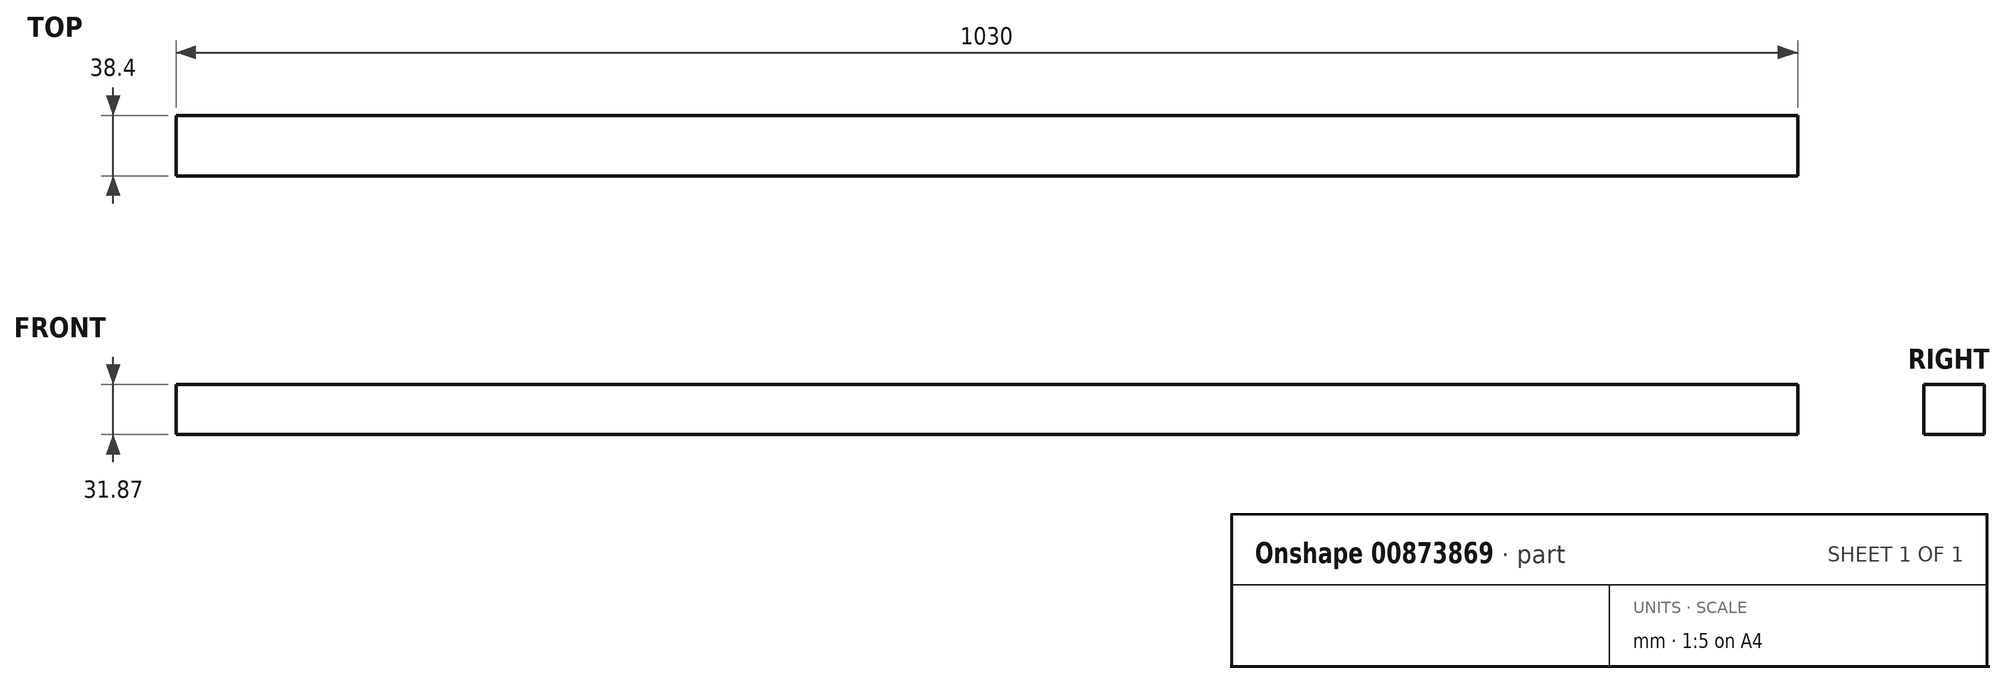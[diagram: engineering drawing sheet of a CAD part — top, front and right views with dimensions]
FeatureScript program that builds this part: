
annotation { "Feature Type Name" : "Feature", "Feature Type Description" : "" }
export const myFeature = defineFeature(function(context is Context, id is Id, definition is map)
    precondition{}
    {
        {
            var Q0;
            Q0=qCreatedBy(makeId("Right.planeOp"),FACE);
            var sketch = newSketch(context, id + "F0", { "sketchPlane" : qUnion([Q0])});
            skLineSegment(sketch, "E0.bottom", {"start": v(0, 0) * mm, "end": v(38.4, 0) * mm});
            skLineSegment(sketch, "E0.top", {"start": v(0, 31.87) * mm, "end": v(38.4, 31.87) * mm});
            skLineSegment(sketch, "E0.left", {"start": v(0, 0) * mm, "end": v(0, 31.87) * mm});
            skLineSegment(sketch, "E0.right", {"start": v(38.4, 0) * mm, "end": v(38.4, 31.87) * mm});
            skSolve(sketch);
        }
        {
            var Q0;
            Q0=makeQuery(id+"F0.imprint","IMPRINT",FACE,{"disambiguationData":[TD([[makeQuery(id+"F0.imprint","IMPRINT",EDGE,{"derivedFrom":sQuery(id+"F0.wireOp",EDGE,"E0.bottom")}),1.0]])]});
            extrude(context, id + "F1", {"entities" : qUnion([Q0]), "depth" : 1030 * mm, "offsetDistance" : 25 * mm});
        }
    });
